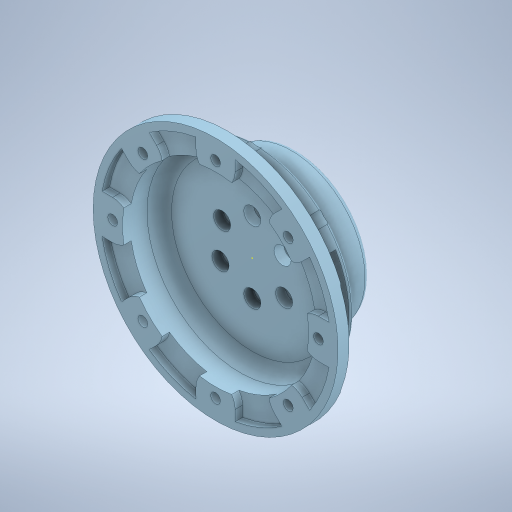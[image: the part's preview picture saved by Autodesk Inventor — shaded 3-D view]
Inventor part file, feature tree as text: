
AUTODESK INVENTOR PART (.ipt)
format: ipt  version: 2023.2 (Build 272271000, 271)  size: 586,752 bytes
history: mixed  units: in
note: dims shown in document units (in); Inventor stores cm internally (conversion verified against a paired STEP export)
features: sketch x6, extrude x5, fillet x2, plane x1, imported_body x1
ambient origin geometry x8: Origin, YZ Plane, XZ Plane, XY Plane, X Axis, Y Axis, Z Axis, Center Point
bodies: Solid1 (imported_parasolid), Body1 (imported_parasolid)
feature tree (15):
  sketch  "Boceto1"  dims[d0=1.9685in d1=0.9562in d2=0.0in d8=0.0787in]
  plane  "Plano de trabajo1"
  extrude  "Extrusión1"  Depth=0.0787in TaperAngle=0.0deg
  fillet  "Empalme1"  Radius=0.0787in
  extrude  "Extrusión4"  Depth=0.6437in TaperAngle=0.0deg
  extrude  "Extrusión5"  Depth=0.6299in TaperAngle=0.0deg
  extrude  "Extrusión6"  Depth=0.2756in
  extrude  "Extrusión7"  Depth=0.2756in
  fillet  "Empalme2"  Radius=0.2756in
  sketch  "Boceto2"  dims[d10=0.2756in d11=0.6437in d12=0.0in]
  sketch  "Boceto5"  dims[d13=0.6299in d14=0.0in d15=2.4424in d16=0.0in]
  sketch  "Boceto6"  dims[d17=0.2756in d18=0.2756in]
  sketch  "Boceto7"  dims[d19=0.2756in d20=0.2756in d21=0.2756in]
  sketch  "Boceto8"  dims[d22=0.2756in d23=0.1575in d24=0.0in d25=0.2756in d26=0.2756in d27=0.2756in d28=0.2756in d29=0.2756in d30=0.2756in d31=0.0787in d3=0.0197in d4=1.9685in]
  imported_body  NMx_Import_Brep_tag  [imported B-rep: ~35 faces, bbox_mm=[80.958333, 80.958333, 28.1]]
